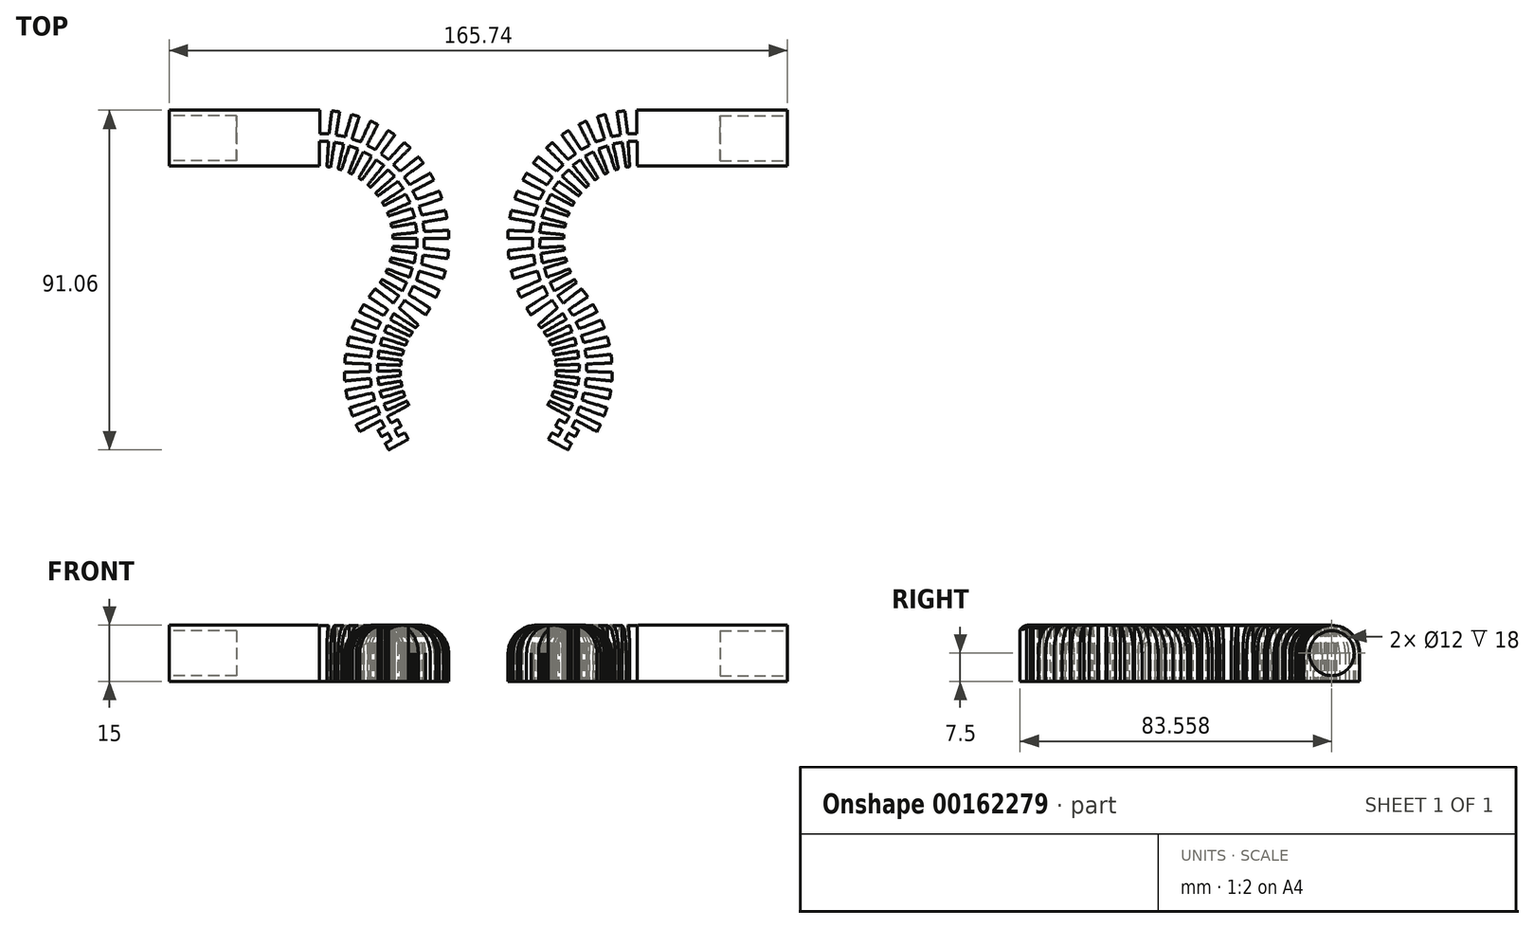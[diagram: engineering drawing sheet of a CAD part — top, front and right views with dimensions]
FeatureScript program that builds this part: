
annotation { "Feature Type Name" : "Feature", "Feature Type Description" : "" }
export const myFeature = defineFeature(function(context is Context, id is Id, definition is map)
    precondition{}
    {
        {
            var Q0;
            Q0=qCreatedBy(makeId("Top.planeOp"),FACE);
            var sketch = newSketch(context, id + "F0", { "sketchPlane" : qUnion([Q0])});
            skLineSegment(sketch, "E0", {"start": v(-77.87, 42.79) * mm, "end": v(-37.87, 42.79) * mm});
            skArc(sketch, "E1", {"start": v(-37.87, 42.79) * mm, "mid": v(-19.7, 31.14) * mm, "end": v(-22.72, 9.78) * mm});
            skArc(sketch, "E2", {"start": v(-22.72, 9.78) * mm, "mid": v(-30.7, -8.67) * mm, "end": v(-26.81, -28.39) * mm});
            skArc(sketch, "E3.0", {"start": v(-11.34, 0) * mm, "mid": v(-15.78, -10.26) * mm, "end": v(-13.63, -21.23) * mm});
            skArc(sketch, "E3.1", {"start": v(-37.87, 57.79) * mm, "mid": v(-6.08, 37.4) * mm, "end": v(-11.34, 0) * mm});
            skLineSegment(sketch, "E3.2", {"start": v(-77.87, 57.79) * mm, "end": v(-37.87, 57.79) * mm});
            skLineSegment(sketch, "E4", {"start": v(-77.87, 57.79) * mm, "end": v(-77.87, 42.79) * mm});
            skLineSegment(sketch, "E5", {"start": v(-77.87, 50.29) * mm, "end": v(-37.87, 50.29) * mm, "construction": true});
            skArc(sketch, "E6", {"start": v(-37.87, 50.29) * mm, "mid": v(-13.36, 34.9) * mm, "end": v(-16.55, 6.14) * mm, "construction": true});
            skArc(sketch, "E7", {"start": v(-16.55, 6.14) * mm, "mid": v(-23.3, -8.75) * mm, "end": v(-20.22, -24.8) * mm, "construction": true});
            skPoint(sketch, "E8.orphan", {"position": v(-19.93, -37.21) * mm});
            skLineSegment(sketch, "E9", {"start": v(-13.63, -21.23) * mm, "end": v(-19.35, -24.33) * mm});
            skLineSegment(sketch, "E10", {"start": v(-21.1, -25.28) * mm, "end": v(-20.15, -27.04) * mm});
            skLineSegment(sketch, "E11", {"start": v(-17.28, -32.31) * mm, "end": v(-15.53, -31.36) * mm});
            skLineSegment(sketch, "E12", {"start": v(-21.9, -28) * mm, "end": v(-20.15, -27.04) * mm});
            skLineSegment(sketch, "E13", {"start": v(-16.63, -25.13) * mm, "end": v(-15.68, -26.89) * mm});
            skLineSegment(sketch, "E14", {"start": v(-15.68, -26.89) * mm, "end": v(-17.44, -27.84) * mm});
            skLineSegment(sketch, "E15", {"start": v(-20.95, -29.75) * mm, "end": v(-21.9, -28) * mm});
            skLineSegment(sketch, "E16", {"start": v(-20, -31.51) * mm, "end": v(-18.24, -30.56) * mm});
            skLineSegment(sketch, "E17", {"start": v(-14.72, -28.65) * mm, "end": v(-13.77, -30.4) * mm});
            skLineSegment(sketch, "E18", {"start": v(-13.77, -30.4) * mm, "end": v(-19.04, -33.27) * mm});
            skLineSegment(sketch, "E19", {"start": v(-19.04, -33.27) * mm, "end": v(-20, -31.51) * mm});
            skLineSegment(sketch, "E20", {"start": v(-20.22, -24.8) * mm, "end": v(-13.33, -37.5) * mm, "construction": true});
            skLineSegment(sketch, "E21.trimOffspring", {"start": v(-20.22, -24.8) * mm, "end": v(-20.22, -24.8) * mm});
            skLineSegment(sketch, "E22.trimOffspring", {"start": v(-21.1, -25.28) * mm, "end": v(-26.81, -28.39) * mm});
            skLineSegment(sketch, "E23.trimOffspring", {"start": v(-18.4, -26.09) * mm, "end": v(-16.63, -25.13) * mm});
            skArc(sketch, "E24.trimOffspring", {"start": v(-15.88, -30.71) * mm, "mid": v(-15.86, -30.73) * mm, "end": v(-15.84, -30.75) * mm, "construction": true});
            skLineSegment(sketch, "E25.trimOffspring", {"start": v(-19.27, -26.56) * mm, "end": v(-19.2, -26.53) * mm});
            skLineSegment(sketch, "E26.trimOffspring", {"start": v(-19.2, -28.8) * mm, "end": v(-20.95, -29.75) * mm});
            skLineSegment(sketch, "E27.trimOffspring", {"start": v(-19.2, -28.8) * mm, "end": v(-18.24, -30.56) * mm});
            skLineSegment(sketch, "E28.trimOffspring", {"start": v(-18.4, -26.09) * mm, "end": v(-19.35, -24.33) * mm});
            skLineSegment(sketch, "E29.trimOffspring", {"start": v(-16.48, -29.6) * mm, "end": v(-14.72, -28.65) * mm});
            skLineSegment(sketch, "E30.trimOffspring", {"start": v(-16.48, -29.6) * mm, "end": v(-17.44, -27.84) * mm});
            skSolve(sketch);
        }
        {
            var Q0;
            Q0=makeQuery(id+"F0.imprint","IMPRINT",FACE,{"disambiguationData":[TD([[makeQuery(id+"F0.imprint","IMPRINT",EDGE,{"derivedFrom":sQuery(id+"F0.wireOp",EDGE,"E0")}),1.0]])]});
            extrude(context, id + "F1", {"entities" : qUnion([Q0]), "depth" : 15 * mm});
        }
        {
            var Q0;
            Q0=makeQuery(id+"F1.opExtrude","CAP_EDGE",EDGE,{"disambiguationData":[OSD([sQuery(id+"F0.wireOp",EDGE,"E0")])],"isStart":false});
            var Q1;
            Q1=makeQuery(id+"F1.opExtrude","CAP_EDGE",EDGE,{"disambiguationData":[OSD([sQuery(id+"F0.wireOp",EDGE,"E3.2")])],"isStart":false});
            fillet(context, id + "F2", {"entities" : qUnion([Q0, Q1]), "radius" : 7.5 * mm, "tangentPropagation" : true, "allowEdgeOverflow" : false});
        }
        {
            var Q0;
            Q0=qCreatedBy(makeId("Top.planeOp"),FACE);
            var sketch = newSketch(context, id + "F3", { "sketchPlane" : qUnion([Q0])});
            skLineSegment(sketch, "E31", {"start": v(-66.67, 50.5) * mm, "end": v(-37.77, 50.5) * mm, "construction": true});
            skArc(sketch, "E32", {"start": v(-37.77, 50.5) * mm, "mid": v(-13.23, 35.1) * mm, "end": v(-16.42, 6.3) * mm, "construction": true});
            skArc(sketch, "E33", {"start": v(-16.42, 6.3) * mm, "mid": v(-22.5, -13.28) * mm, "end": v(-13.17, -31.54) * mm, "construction": true});
            skLineSegment(sketch, "E34.bottom", {"start": v(-37.54, 51.5) * mm, "end": v(-35.04, 51.5) * mm});
            skLineSegment(sketch, "E34.top", {"start": v(-37.54, 59.7) * mm, "end": v(-34.04, 59.7) * mm});
            skLineSegment(sketch, "E34.left", {"start": v(-37.54, 51.5) * mm, "end": v(-37.54, 59.7) * mm});
            skLineSegment(sketch, "E34.right", {"start": v(-35.04, 51.5) * mm, "end": v(-34.04, 59.7) * mm});
            skLineSegment(sketch, "E35.bottom", {"start": v(-37.65, 33.82) * mm, "end": v(-36.15, 33.82) * mm});
            skLineSegment(sketch, "E35.top", {"start": v(-37.65, 49.5) * mm, "end": v(-35.15, 49.5) * mm});
            skLineSegment(sketch, "E35.left", {"start": v(-37.65, 33.82) * mm, "end": v(-37.65, 49.5) * mm});
            skLineSegment(sketch, "E35.right", {"start": v(-36.15, 33.82) * mm, "end": v(-35.15, 49.5) * mm});
            skLineSegment(sketch, "E36.1.0", {"start": v(-30.68, 50.73) * mm, "end": v(-28.42, 58.69) * mm});
            skLineSegment(sketch, "E36.1.1", {"start": v(-33.15, 51.12) * mm, "end": v(-31.88, 59.23) * mm});
            skLineSegment(sketch, "E36.1.2", {"start": v(-34.53, 33.44) * mm, "end": v(-31.1, 48.77) * mm});
            skLineSegment(sketch, "E36.1.3", {"start": v(-36.01, 33.67) * mm, "end": v(-33.58, 49.16) * mm});
            skLineSegment(sketch, "E36.1.4", {"start": v(-31.88, 59.23) * mm, "end": v(-28.42, 58.69) * mm});
            skLineSegment(sketch, "E36.1.5", {"start": v(-33.15, 51.12) * mm, "end": v(-30.68, 50.73) * mm});
            skLineSegment(sketch, "E36.1.6", {"start": v(-33.58, 49.16) * mm, "end": v(-31.1, 48.77) * mm});
            skLineSegment(sketch, "E36.1.7", {"start": v(-36.01, 33.67) * mm, "end": v(-34.53, 33.44) * mm});
            skLineSegment(sketch, "E36.2.0", {"start": v(-26.5, 49.3) * mm, "end": v(-23.03, 56.8) * mm});
            skLineSegment(sketch, "E36.2.1", {"start": v(-28.88, 50.06) * mm, "end": v(-26.37, 57.88) * mm});
            skLineSegment(sketch, "E36.2.2", {"start": v(-32.99, 32.81) * mm, "end": v(-27.23, 47.43) * mm});
            skLineSegment(sketch, "E36.2.3", {"start": v(-34.41, 33.27) * mm, "end": v(-29.6, 48.2) * mm});
            skLineSegment(sketch, "E36.2.4", {"start": v(-26.37, 57.88) * mm, "end": v(-23.03, 56.8) * mm});
            skLineSegment(sketch, "E36.2.5", {"start": v(-28.88, 50.06) * mm, "end": v(-26.5, 49.3) * mm});
            skLineSegment(sketch, "E36.2.6", {"start": v(-29.6, 48.2) * mm, "end": v(-27.23, 47.43) * mm});
            skLineSegment(sketch, "E36.2.7", {"start": v(-34.41, 33.27) * mm, "end": v(-32.99, 32.81) * mm});
            skLineSegment(sketch, "E36.3.0", {"start": v(-22.6, 47.23) * mm, "end": v(-18, 54.11) * mm});
            skLineSegment(sketch, "E36.3.1", {"start": v(-24.83, 48.36) * mm, "end": v(-21.13, 55.69) * mm});
            skLineSegment(sketch, "E36.3.2", {"start": v(-31.56, 31.95) * mm, "end": v(-23.6, 45.5) * mm});
            skLineSegment(sketch, "E36.3.3", {"start": v(-32.9, 32.63) * mm, "end": v(-25.83, 46.63) * mm});
            skLineSegment(sketch, "E36.3.4", {"start": v(-21.13, 55.69) * mm, "end": v(-18, 54.11) * mm});
            skLineSegment(sketch, "E36.3.5", {"start": v(-24.83, 48.36) * mm, "end": v(-22.6, 47.23) * mm});
            skLineSegment(sketch, "E36.3.6", {"start": v(-25.83, 46.63) * mm, "end": v(-23.6, 45.5) * mm});
            skLineSegment(sketch, "E36.3.7", {"start": v(-32.9, 32.63) * mm, "end": v(-31.56, 31.95) * mm});
            skLineSegment(sketch, "E36.4.0", {"start": v(-19.06, 44.59) * mm, "end": v(-13.45, 50.67) * mm});
            skLineSegment(sketch, "E36.4.1", {"start": v(-21.09, 46.05) * mm, "end": v(-16.3, 52.71) * mm});
            skLineSegment(sketch, "E36.4.2", {"start": v(-30.28, 30.88) * mm, "end": v(-20.32, 43.03) * mm});
            skLineSegment(sketch, "E36.4.3", {"start": v(-31.5, 31.76) * mm, "end": v(-22.35, 44.5) * mm});
            skLineSegment(sketch, "E36.4.4", {"start": v(-16.3, 52.71) * mm, "end": v(-13.45, 50.67) * mm});
            skLineSegment(sketch, "E36.4.5", {"start": v(-21.09, 46.05) * mm, "end": v(-19.06, 44.59) * mm});
            skLineSegment(sketch, "E36.4.6", {"start": v(-22.35, 44.5) * mm, "end": v(-20.32, 43.03) * mm});
            skLineSegment(sketch, "E36.4.7", {"start": v(-31.5, 31.76) * mm, "end": v(-30.28, 30.88) * mm});
            skLineSegment(sketch, "E36.5.0", {"start": v(-15.97, 41.42) * mm, "end": v(-9.5, 46.56) * mm});
            skLineSegment(sketch, "E36.5.1", {"start": v(-17.75, 43.18) * mm, "end": v(-11.98, 49.02) * mm});
            skLineSegment(sketch, "E36.5.2", {"start": v(-29.19, 29.63) * mm, "end": v(-17.46, 40.08) * mm});
            skLineSegment(sketch, "E36.5.3", {"start": v(-30.26, 30.68) * mm, "end": v(-19.24, 41.84) * mm});
            skLineSegment(sketch, "E36.5.4", {"start": v(-11.98, 49.02) * mm, "end": v(-9.5, 46.56) * mm});
            skLineSegment(sketch, "E36.5.5", {"start": v(-17.75, 43.18) * mm, "end": v(-15.97, 41.42) * mm});
            skLineSegment(sketch, "E36.5.6", {"start": v(-19.24, 41.84) * mm, "end": v(-17.46, 40.08) * mm});
            skLineSegment(sketch, "E36.5.7", {"start": v(-30.26, 30.68) * mm, "end": v(-29.19, 29.63) * mm});
            skLineSegment(sketch, "E36.6.0", {"start": v(-13.41, 37.82) * mm, "end": v(-6.21, 41.9) * mm});
            skLineSegment(sketch, "E36.6.1", {"start": v(-14.9, 39.83) * mm, "end": v(-8.3, 44.7) * mm});
            skLineSegment(sketch, "E36.6.2", {"start": v(-28.3, 28.22) * mm, "end": v(-15.1, 36.73) * mm});
            skLineSegment(sketch, "E36.6.3", {"start": v(-29.2, 29.43) * mm, "end": v(-16.58, 38.74) * mm});
            skLineSegment(sketch, "E36.6.4", {"start": v(-8.3, 44.7) * mm, "end": v(-6.21, 41.9) * mm});
            skLineSegment(sketch, "E36.6.5", {"start": v(-14.9, 39.83) * mm, "end": v(-13.41, 37.82) * mm});
            skLineSegment(sketch, "E36.6.6", {"start": v(-16.58, 38.74) * mm, "end": v(-15.1, 36.73) * mm});
            skLineSegment(sketch, "E36.6.7", {"start": v(-29.2, 29.43) * mm, "end": v(-28.3, 28.22) * mm});
            skLineSegment(sketch, "E36.7.0", {"start": v(-11.45, 33.86) * mm, "end": v(-3.7, 36.77) * mm});
            skLineSegment(sketch, "E36.7.1", {"start": v(-12.6, 36.08) * mm, "end": v(-5.32, 39.87) * mm});
            skLineSegment(sketch, "E36.7.2", {"start": v(-27.64, 26.69) * mm, "end": v(-13.27, 33.04) * mm});
            skLineSegment(sketch, "E36.7.3", {"start": v(-28.34, 28.02) * mm, "end": v(-14.43, 35.26) * mm});
            skLineSegment(sketch, "E36.7.4", {"start": v(-5.32, 39.87) * mm, "end": v(-3.7, 36.77) * mm});
            skLineSegment(sketch, "E36.7.5", {"start": v(-12.6, 36.08) * mm, "end": v(-11.45, 33.86) * mm});
            skLineSegment(sketch, "E36.7.6", {"start": v(-14.43, 35.26) * mm, "end": v(-13.27, 33.04) * mm});
            skLineSegment(sketch, "E36.7.7", {"start": v(-28.34, 28.02) * mm, "end": v(-27.64, 26.69) * mm});
            skLineSegment(sketch, "E36.8.0", {"start": v(-10.12, 29.65) * mm, "end": v(-2.02, 31.32) * mm});
            skLineSegment(sketch, "E36.8.1", {"start": v(-10.91, 32.02) * mm, "end": v(-3.13, 34.63) * mm});
            skLineSegment(sketch, "E36.8.2", {"start": v(-27.23, 25.08) * mm, "end": v(-12.05, 29.12) * mm});
            skLineSegment(sketch, "E36.8.3", {"start": v(-27.7, 26.5) * mm, "end": v(-12.84, 31.5) * mm});
            skLineSegment(sketch, "E36.8.4", {"start": v(-3.13, 34.63) * mm, "end": v(-2.02, 31.32) * mm});
            skLineSegment(sketch, "E36.8.5", {"start": v(-10.91, 32.02) * mm, "end": v(-10.12, 29.65) * mm});
            skLineSegment(sketch, "E36.8.6", {"start": v(-12.84, 31.5) * mm, "end": v(-12.05, 29.12) * mm});
            skLineSegment(sketch, "E36.8.7", {"start": v(-27.7, 26.5) * mm, "end": v(-27.23, 25.08) * mm});
            skLineSegment(sketch, "E36.9.0", {"start": v(-9.46, 25.28) * mm, "end": v(-1.2, 25.67) * mm});
            skLineSegment(sketch, "E36.9.1", {"start": v(-9.88, 27.74) * mm, "end": v(-1.78, 29.12) * mm});
            skLineSegment(sketch, "E36.9.2", {"start": v(-27.07, 23.42) * mm, "end": v(-11.45, 25.06) * mm});
            skLineSegment(sketch, "E36.9.3", {"start": v(-27.33, 24.9) * mm, "end": v(-11.87, 27.52) * mm});
            skLineSegment(sketch, "E36.9.4", {"start": v(-1.78, 29.12) * mm, "end": v(-1.2, 25.67) * mm});
            skLineSegment(sketch, "E36.9.5", {"start": v(-9.88, 27.74) * mm, "end": v(-9.46, 25.28) * mm});
            skLineSegment(sketch, "E36.9.6", {"start": v(-11.87, 27.52) * mm, "end": v(-11.45, 25.06) * mm});
            skLineSegment(sketch, "E36.9.7", {"start": v(-27.33, 24.9) * mm, "end": v(-27.07, 23.42) * mm});
            skLineSegment(sketch, "E36.10.0", {"start": v(-9.48, 20.86) * mm, "end": v(-1.26, 19.96) * mm});
            skLineSegment(sketch, "E36.10.1", {"start": v(-9.51, 23.36) * mm, "end": v(-1.3, 23.46) * mm});
            skLineSegment(sketch, "E36.10.2", {"start": v(-27.18, 21.75) * mm, "end": v(-11.48, 20.95) * mm});
            skLineSegment(sketch, "E36.10.3", {"start": v(-27.2, 23.25) * mm, "end": v(-11.52, 23.45) * mm});
            skLineSegment(sketch, "E36.10.4", {"start": v(-1.3, 23.46) * mm, "end": v(-1.26, 19.96) * mm});
            skLineSegment(sketch, "E36.10.5", {"start": v(-9.51, 23.36) * mm, "end": v(-9.48, 20.86) * mm});
            skLineSegment(sketch, "E36.10.6", {"start": v(-11.52, 23.45) * mm, "end": v(-11.48, 20.95) * mm});
            skLineSegment(sketch, "E36.10.7", {"start": v(-27.2, 23.25) * mm, "end": v(-27.18, 21.75) * mm});
            skLineSegment(sketch, "E36.11.0", {"start": v(-10.2, 16.5) * mm, "end": v(-2.21, 14.34) * mm});
            skLineSegment(sketch, "E36.11.1", {"start": v(-9.84, 18.97) * mm, "end": v(-1.71, 17.8) * mm});
            skLineSegment(sketch, "E36.11.2", {"start": v(-27.54, 20.13) * mm, "end": v(-12.16, 16.9) * mm});
            skLineSegment(sketch, "E36.11.3", {"start": v(-27.32, 21.61) * mm, "end": v(-11.8, 19.37) * mm});
            skLineSegment(sketch, "E36.11.4", {"start": v(-1.71, 17.8) * mm, "end": v(-2.21, 14.34) * mm});
            skLineSegment(sketch, "E36.11.5", {"start": v(-9.84, 18.97) * mm, "end": v(-10.2, 16.5) * mm});
            skLineSegment(sketch, "E36.11.6", {"start": v(-11.8, 19.37) * mm, "end": v(-12.16, 16.9) * mm});
            skLineSegment(sketch, "E36.11.7", {"start": v(-27.32, 21.61) * mm, "end": v(-27.54, 20.13) * mm});
            skLineSegment(sketch, "E36.12.0", {"start": v(-11.58, 12.3) * mm, "end": v(-4.03, 8.93) * mm});
            skLineSegment(sketch, "E36.12.1", {"start": v(-10.84, 14.69) * mm, "end": v(-3, 12.27) * mm});
            skLineSegment(sketch, "E36.12.2", {"start": v(-28.14, 18.58) * mm, "end": v(-13.45, 13) * mm});
            skLineSegment(sketch, "E36.12.3", {"start": v(-27.7, 20.01) * mm, "end": v(-12.72, 15.39) * mm});
            skLineSegment(sketch, "E36.12.4", {"start": v(-3, 12.27) * mm, "end": v(-4.03, 8.93) * mm});
            skLineSegment(sketch, "E36.12.5", {"start": v(-10.84, 14.69) * mm, "end": v(-11.58, 12.3) * mm});
            skLineSegment(sketch, "E36.12.6", {"start": v(-12.72, 15.39) * mm, "end": v(-13.45, 13) * mm});
            skLineSegment(sketch, "E36.12.7", {"start": v(-27.7, 20.01) * mm, "end": v(-28.14, 18.58) * mm});
            skLineSegment(sketch, "E36.13.0", {"start": v(-13.6, 8.37) * mm, "end": v(-6.66, 3.86) * mm});
            skLineSegment(sketch, "E36.13.1", {"start": v(-12.5, 10.61) * mm, "end": v(-5.12, 7) * mm});
            skLineSegment(sketch, "E36.13.2", {"start": v(-28.98, 17.14) * mm, "end": v(-15.34, 9.35) * mm});
            skLineSegment(sketch, "E36.13.3", {"start": v(-28.32, 18.49) * mm, "end": v(-14.24, 11.6) * mm});
            skLineSegment(sketch, "E36.13.4", {"start": v(-5.12, 7) * mm, "end": v(-6.66, 3.86) * mm});
            skLineSegment(sketch, "E36.13.5", {"start": v(-12.5, 10.61) * mm, "end": v(-13.6, 8.37) * mm});
            skLineSegment(sketch, "E36.13.6", {"start": v(-14.24, 11.6) * mm, "end": v(-15.34, 9.35) * mm});
            skLineSegment(sketch, "E36.13.7", {"start": v(-28.32, 18.49) * mm, "end": v(-28.98, 17.14) * mm});
            skLineSegment(sketch, "E36.14.0", {"start": v(-16.2, 4.8) * mm, "end": v(-10.04, -0.73) * mm});
            skLineSegment(sketch, "E36.14.1", {"start": v(-14.76, 6.84) * mm, "end": v(-8.03, 2.13) * mm});
            skLineSegment(sketch, "E36.14.2", {"start": v(-30.04, 15.85) * mm, "end": v(-17.77, 6.04) * mm});
            skLineSegment(sketch, "E36.14.3", {"start": v(-29.18, 17.08) * mm, "end": v(-16.33, 8.08) * mm});
            skLineSegment(sketch, "E36.14.4", {"start": v(-8.03, 2.13) * mm, "end": v(-10.04, -0.73) * mm});
            skLineSegment(sketch, "E36.14.5", {"start": v(-14.76, 6.84) * mm, "end": v(-16.2, 4.8) * mm});
            skLineSegment(sketch, "E36.14.6", {"start": v(-16.33, 8.08) * mm, "end": v(-17.77, 6.04) * mm});
            skLineSegment(sketch, "E36.14.7", {"start": v(-29.18, 17.08) * mm, "end": v(-30.04, 15.85) * mm});
            skLineSegment(sketch, "E36.anchor1", {"start": v(-37.77, 23.24) * mm, "end": v(-37.65, 33.82) * mm, "construction": true});
            skLineSegment(sketch, "E36.anchor2", {"start": v(-37.77, 23.24) * mm, "end": v(-29.18, 17.08) * mm, "construction": true});
            skSolve(sketch);
        }
        {
            var Q0;
            Q0=qSketchRegion(id+"F3",true);
            extrude(context, id + "F4", {"entities" : qUnion([Q0]), "operationType" : NewBodyOperationType.REMOVE, "endBound" : BoundingType.THROUGH_ALL, "depth" : 25 * mm});
        }
        {
            var Q0;
            Q0=qCreatedBy(makeId("Top.planeOp"),FACE);
            var sketch = newSketch(context, id + "F5", { "sketchPlane" : qUnion([Q0])});
            skLineSegment(sketch, "E37", {"start": v(-67.85, 51.08) * mm, "end": v(-38.46, 51.08) * mm, "construction": true});
            skArc(sketch, "E38", {"start": v(-38.46, 51.08) * mm, "mid": v(-13.5, 35.42) * mm, "end": v(-16.74, 6.13) * mm, "construction": true});
            skArc(sketch, "E39", {"start": v(-16.74, 6.13) * mm, "mid": v(-22.93, -13.8) * mm, "end": v(-13.43, -32.37) * mm, "construction": true});
            skLineSegment(sketch, "E40", {"start": v(4.62, -11.43) * mm, "end": v(-17.67, 3.3) * mm});
            skLineSegment(sketch, "E41", {"start": v(-26.5, 9.14) * mm, "end": v(-27.76, 6.87) * mm});
            skLineSegment(sketch, "E42", {"start": v(-27.76, 6.87) * mm, "end": v(-20.38, 2.7) * mm});
            skLineSegment(sketch, "E43", {"start": v(-17.67, 3.3) * mm, "end": v(-18.58, 1.68) * mm});
            skLineSegment(sketch, "E44", {"start": v(-20.38, 2.7) * mm, "end": v(-19.28, 4.37) * mm});
            skLineSegment(sketch, "E45.trimOffspring", {"start": v(-19.28, 4.37) * mm, "end": v(-26.5, 9.14) * mm});
            skLineSegment(sketch, "E46.trimOffspring", {"start": v(-18.58, 1.68) * mm, "end": v(4.62, -11.43) * mm});
            skLineSegment(sketch, "E47.1.0", {"start": v(4.62, -11.43) * mm, "end": v(-19.45, 0.15) * mm});
            skLineSegment(sketch, "E47.1.1", {"start": v(-28.99, 4.74) * mm, "end": v(-29.94, 2.32) * mm});
            skLineSegment(sketch, "E47.1.2", {"start": v(-20.14, -1.58) * mm, "end": v(4.62, -11.43) * mm});
            skLineSegment(sketch, "E47.1.3", {"start": v(-29.94, 2.32) * mm, "end": v(-22.07, -0.81) * mm});
            skLineSegment(sketch, "E47.1.4", {"start": v(-19.45, 0.15) * mm, "end": v(-20.14, -1.58) * mm});
            skLineSegment(sketch, "E47.1.5", {"start": v(-21.2, 1) * mm, "end": v(-28.99, 4.74) * mm});
            skLineSegment(sketch, "E47.1.6", {"start": v(-22.07, -0.81) * mm, "end": v(-21.2, 1) * mm});
            skLineSegment(sketch, "E47.2.0", {"start": v(4.62, -11.43) * mm, "end": v(-20.8, -3.21) * mm});
            skLineSegment(sketch, "E47.2.1", {"start": v(-30.87, 0.04) * mm, "end": v(-31.48, -2.48) * mm});
            skLineSegment(sketch, "E47.2.2", {"start": v(-21.25, -5.02) * mm, "end": v(4.62, -11.43) * mm});
            skLineSegment(sketch, "E47.2.3", {"start": v(-31.48, -2.48) * mm, "end": v(-23.26, -4.52) * mm});
            skLineSegment(sketch, "E47.2.4", {"start": v(-20.8, -3.21) * mm, "end": v(-21.25, -5.02) * mm});
            skLineSegment(sketch, "E47.2.5", {"start": v(-22.64, -2.62) * mm, "end": v(-30.87, 0.04) * mm});
            skLineSegment(sketch, "E47.2.6", {"start": v(-23.26, -4.52) * mm, "end": v(-22.64, -2.62) * mm});
            skLineSegment(sketch, "E47.3.0", {"start": v(4.62, -11.43) * mm, "end": v(-21.68, -6.73) * mm});
            skLineSegment(sketch, "E47.3.1", {"start": v(-32.1, -4.86) * mm, "end": v(-32.36, -7.45) * mm});
            skLineSegment(sketch, "E47.3.2", {"start": v(-21.88, -8.58) * mm, "end": v(4.62, -11.43) * mm});
            skLineSegment(sketch, "E47.3.3", {"start": v(-32.36, -7.45) * mm, "end": v(-23.93, -8.36) * mm});
            skLineSegment(sketch, "E47.3.4", {"start": v(-21.68, -6.73) * mm, "end": v(-21.88, -8.58) * mm});
            skLineSegment(sketch, "E47.3.5", {"start": v(-23.58, -6.39) * mm, "end": v(-32.1, -4.86) * mm});
            skLineSegment(sketch, "E47.3.6", {"start": v(-23.93, -8.36) * mm, "end": v(-23.58, -6.39) * mm});
            skLineSegment(sketch, "E47.4.0", {"start": v(4.62, -11.43) * mm, "end": v(-22.07, -10.33) * mm});
            skLineSegment(sketch, "E47.4.1", {"start": v(-32.64, -9.9) * mm, "end": v(-32.56, -12.5) * mm});
            skLineSegment(sketch, "E47.4.2", {"start": v(-22.02, -12.19) * mm, "end": v(4.62, -11.43) * mm});
            skLineSegment(sketch, "E47.4.3", {"start": v(-32.56, -12.5) * mm, "end": v(-24.09, -12.25) * mm});
            skLineSegment(sketch, "E47.4.4", {"start": v(-22.07, -10.33) * mm, "end": v(-22.02, -12.19) * mm});
            skLineSegment(sketch, "E47.4.5", {"start": v(-24, -10.25) * mm, "end": v(-32.64, -9.9) * mm});
            skLineSegment(sketch, "E47.4.6", {"start": v(-24.09, -12.25) * mm, "end": v(-24, -10.25) * mm});
            skLineSegment(sketch, "E47.5.0", {"start": v(4.62, -11.43) * mm, "end": v(-21.98, -13.95) * mm});
            skLineSegment(sketch, "E47.5.1", {"start": v(-32.5, -14.95) * mm, "end": v(-32.07, -17.51) * mm});
            skLineSegment(sketch, "E47.5.2", {"start": v(-21.67, -15.79) * mm, "end": v(4.62, -11.43) * mm});
            skLineSegment(sketch, "E47.5.3", {"start": v(-32.07, -17.51) * mm, "end": v(-23.71, -16.13) * mm});
            skLineSegment(sketch, "E47.5.4", {"start": v(-21.98, -13.95) * mm, "end": v(-21.67, -15.79) * mm});
            skLineSegment(sketch, "E47.5.5", {"start": v(-23.9, -14.13) * mm, "end": v(-32.5, -14.95) * mm});
            skLineSegment(sketch, "E47.5.6", {"start": v(-23.71, -16.13) * mm, "end": v(-23.9, -14.13) * mm});
            skLineSegment(sketch, "E47.6.0", {"start": v(4.62, -11.43) * mm, "end": v(-21.39, -17.53) * mm});
            skLineSegment(sketch, "E47.6.1", {"start": v(-31.69, -19.94) * mm, "end": v(-30.91, -22.42) * mm});
            skLineSegment(sketch, "E47.6.2", {"start": v(-20.84, -19.3) * mm, "end": v(4.62, -11.43) * mm});
            skLineSegment(sketch, "E47.6.3", {"start": v(-30.91, -22.42) * mm, "end": v(-22.82, -19.92) * mm});
            skLineSegment(sketch, "E47.6.4", {"start": v(-21.39, -17.53) * mm, "end": v(-20.84, -19.3) * mm});
            skLineSegment(sketch, "E47.6.5", {"start": v(-23.27, -17.97) * mm, "end": v(-31.69, -19.94) * mm});
            skLineSegment(sketch, "E47.6.6", {"start": v(-22.82, -19.92) * mm, "end": v(-23.27, -17.97) * mm});
            skLineSegment(sketch, "E47.7.0", {"start": v(4.62, -11.43) * mm, "end": v(-20.32, -20.99) * mm});
            skLineSegment(sketch, "E47.7.1", {"start": v(-30.2, -24.78) * mm, "end": v(-29.1, -27.13) * mm});
            skLineSegment(sketch, "E47.7.2", {"start": v(-19.54, -22.68) * mm, "end": v(4.62, -11.43) * mm});
            skLineSegment(sketch, "E47.7.3", {"start": v(-29.1, -27.13) * mm, "end": v(-21.41, -23.55) * mm});
            skLineSegment(sketch, "E47.7.4", {"start": v(-20.32, -20.99) * mm, "end": v(-19.54, -22.68) * mm});
            skLineSegment(sketch, "E47.7.5", {"start": v(-22.13, -21.68) * mm, "end": v(-30.2, -24.78) * mm});
            skLineSegment(sketch, "E47.7.6", {"start": v(-21.41, -23.55) * mm, "end": v(-22.13, -21.68) * mm});
            skLineSegment(sketch, "E47.8.0", {"start": v(4.62, -11.43) * mm, "end": v(-18.8, -24.28) * mm});
            skLineSegment(sketch, "E47.8.1", {"start": v(-28.08, -29.37) * mm, "end": v(-26.66, -31.55) * mm});
            skLineSegment(sketch, "E47.8.2", {"start": v(-12.16, -22.22) * mm, "end": v(4.62, -11.43) * mm});
            skLineSegment(sketch, "E47.anchor1", {"start": v(4.62, -11.43) * mm, "end": v(-27.76, 6.87) * mm, "construction": true});
            skLineSegment(sketch, "E48", {"start": v(-18.8, -24.28) * mm, "end": v(-20.5, -25.2) * mm});
            skLineSegment(sketch, "E49", {"start": v(-10.79, -24.36) * mm, "end": v(-12.16, -22.22) * mm});
            skPoint(sketch, "E50.orphan", {"position": v(-17.8, -25.84) * mm});
            skSolve(sketch);
        }
        {
            var Q0;
            Q0=qSketchRegion(id+"F5",true);
            extrude(context, id + "F6", {"entities" : qUnion([Q0]), "operationType" : NewBodyOperationType.REMOVE, "depth" : 25 * mm});
        }
        {
            var Q0;
            Q0=qCreatedBy(makeId("Right.planeOp"),FACE);
            cPlane(context, id + "F7", {"entities" : qUnion([Q0]), "cplaneType" : CPlaneType.OFFSET, "offset" : 5 * mm, "width" : 150 * mm, "height" : 150 * mm});
        }
        {
            var Q0;
            Q0=makeQuery(id+"F1.opExtrude","SWEPT_FACE",FACE,{"disambiguationData":[OSD([sQuery(id+"F0.wireOp",EDGE,"E4")])]});
            var sketch = newSketch(context, id + "F8", { "sketchPlane" : qUnion([Q0])});
            skCircle(sketch, "E51", {"center": v(-50.29, 7.5) * mm, "radius": 6 * mm});
            skSolve(sketch);
        }
        {
            var Q0;
            Q0 = qSketchRegion(id + "F8", true);
            extrude(context, id + "F9", {"entities" : qUnion([Q0]), "operationType" : NewBodyOperationType.REMOVE, "oppositeDirection" : true, "depth" : 18 * mm});
        }
        {
            var Q0;
            Q0=makeQuery(id+"F1.opExtrude","SWEPT_BODY",BODY,{"disambiguationData":[OSD([sQuery(id+"F0.wireOp",EDGE,"E0"),sQuery(id+"F0.wireOp",EDGE,"E1"),sQuery(id+"F0.wireOp",EDGE,"E2"),sQuery(id+"F0.wireOp",EDGE,"E3.0"),sQuery(id+"F0.wireOp",EDGE,"E3.1"),sQuery(id+"F0.wireOp",EDGE,"E3.2"),sQuery(id+"F0.wireOp",EDGE,"E4"),sQuery(id+"F0.wireOp",EDGE,"nq4ayG1A-BEII-Ck47-MEMu-i0klakBZy7zp"),sQuery(id+"F0.wireOp",EDGE,"GCjqfLIw-4tHJ-K3OX-aefr-dLJVnuN13NiZ"),sQuery(id+"F0.wireOp",EDGE,"l1ZJvOk0-Q8qS-XGLS-OYS3-i8Vxw84lKiZL"),sQuery(id+"F0.wireOp",EDGE,"ZiP1sOX9-bYlX-xstd-Ms2b-J46Trs5Hx3Kg"),sQuery(id+"F0.wireOp",EDGE,"uGIeJlpd-eJdm-53kQ-2pg1-VMkY2LoaLV9I"),sQuery(id+"F0.wireOp",EDGE,"6MbWeA74-1lYz-mAYS-gQn7-LtqPxN3htQAn"),sQuery(id+"F0.wireOp",EDGE,"d2638795-5e75-42e8-83a0-a97a01c8cce5.1.0.0"),sQuery(id+"F0.wireOp",EDGE,"d2638795-5e75-42e8-83a0-a97a01c8cce5.1.0.1"),sQuery(id+"F0.wireOp",EDGE,"d2638795-5e75-42e8-83a0-a97a01c8cce5.1.0.2"),sQuery(id+"F0.wireOp",EDGE,"d2638795-5e75-42e8-83a0-a97a01c8cce5.1.0.3"),sQuery(id+"F0.wireOp",EDGE,"d2638795-5e75-42e8-83a0-a97a01c8cce5.2.0.0"),sQuery(id+"F0.wireOp",EDGE,"d2638795-5e75-42e8-83a0-a97a01c8cce5.2.0.1"),sQuery(id+"F0.wireOp",EDGE,"d2638795-5e75-42e8-83a0-a97a01c8cce5.2.0.2"),sQuery(id+"F0.wireOp",EDGE,"UdGBiLtL-GqYD-LhIq-0uLs-0zLlh5hnKIaR"),sQuery(id+"F0.wireOp",EDGE,"ollGR6ow-8rVX-IJGJ-55rA-00sAogdXzBgo"),sQuery(id+"F0.wireOp",EDGE,"tCnrbg7b-z0gW-49eu-LeZs-t3sS9Zh2jKse"),sQuery(id+"F0.wireOp",EDGE,"xupdygBY-U3bi-xskL-PjHV-4gtycQiRlDUM"),sQuery(id+"F0.wireOp",EDGE,"99550748-6441-42e6-a354-efeb979eb10f.trimOffspring"),sQuery(id+"F0.wireOp",EDGE,"6ae180e2-d7c2-40ba-b26b-353b6077b774.trimOffspring"),sQuery(id+"F0.wireOp",EDGE,"5a5240f6-9525-4f2b-be8e-03961fa82591.trimOffspring"),sQuery(id+"F0.wireOp",EDGE,"3hIQTL7V-xpQ2-J39L-0Z3X-DxR6HIriGl3R"),sQuery(id+"F0.wireOp",EDGE,"20be2ded-8293-44c6-9252-7684dbbaaef9.trimOffspring"),sQuery(id+"F0.wireOp",EDGE,"c5dca16e-479a-4c81-8bea-56400dd3cf5a.trimOffspring"),sQuery(id+"F0.wireOp",EDGE,"37eedf12-70ad-453d-9fc5-f9742eb4f07a.trimOffspring"),sQuery(id+"F0.wireOp",EDGE,"881e6b71-be12-4d94-890d-cbd95138921e.trimOffspring"),sQuery(id+"F0.wireOp",EDGE,"6d832191-4b66-459f-972c-d8f047ed0479.trimOffspring"),sQuery(id+"F0.wireOp",EDGE,"e0b83be3-b50d-49af-8219-7c6f9b234a88.trimOffspring"),sQuery(id+"F0.wireOp",EDGE,"78cc0b57-e64d-414c-a589-5e33aff0da8e.trimOffspring"),sQuery(id+"F0.wireOp",EDGE,"LBatumNK-q2G8-Lr65-CaIH-jCYntoWbxu4t")])]});
            var Q1;
            Q1=qCreatedBy(id+"F7.planeOp",FACE);
            mirror(context, id + "F10", {"entities" : qUnion([Q0]), "mirrorPlane" : qUnion([Q1])});
        }
    });
